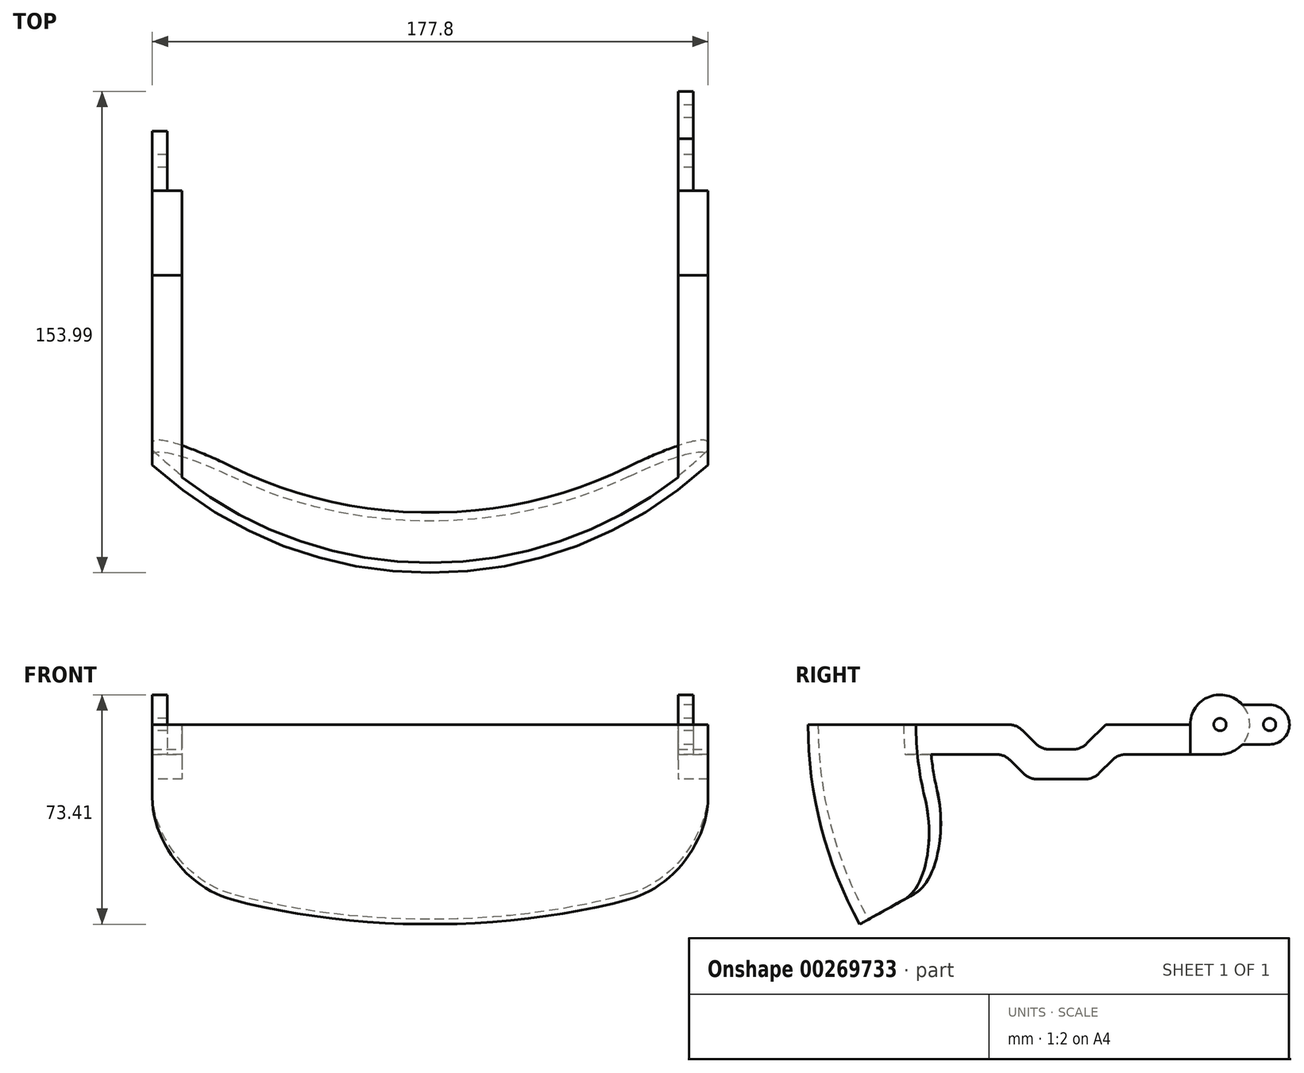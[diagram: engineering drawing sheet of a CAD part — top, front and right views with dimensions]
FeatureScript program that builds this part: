
annotation { "Feature Type Name" : "Feature", "Feature Type Description" : "" }
export const myFeature = defineFeature(function(context is Context, id is Id, definition is map)
    precondition{}
    {
        {
            var Q0;
            Q0=qCreatedBy(makeId("Right.planeOp"),FACE);
            var sketch = newSketch(context, id + "F0", { "sketchPlane" : qUnion([Q0])});
            skArc(sketch, "E0", {"start": v(0, 131.76) * mm, "mid": v(-131.76, 0) * mm, "end": v(0, -131.76) * mm});
            skArc(sketch, "E1", {"start": v(0, 128.59) * mm, "mid": v(-128.59, 0) * mm, "end": v(0, -128.59) * mm});
            skLineSegment(sketch, "E2", {"start": v(0, 131.76) * mm, "end": v(0, 0) * mm});
            skLineSegment(sketch, "E3.trimOffspring", {"start": v(0, -128.59) * mm, "end": v(0, -131.76) * mm});
            skPoint(sketch, "E4.orphan", {"position": v(0, 139.69) * mm});
            skSolve(sketch);
        }
        {
            var Q0;
            Q0 = qSketchRegion(id + "F0", true);
            var Q1;
            Q1=sQuery(id+"F0.wireOp",EDGE,"E2");
            revolve(context, id + "F1", {"entities" : qUnion([Q0]), "axis" : qUnion([Q1]), "revolveType" : RevolveType.FULL});
        }
        {
            var Q0;
            Q0=qCreatedBy(makeId("Front.planeOp"),FACE);
            var sketch = newSketch(context, id + "F2", { "sketchPlane" : qUnion([Q0])});
            skLineSegment(sketch, "E5.left", {"start": v(88.9, 154.45) * mm, "end": v(88.9, -154.45) * mm});
            skLineSegment(sketch, "E5.right", {"start": v(-88.9, 154.45) * mm, "end": v(-88.9, -154.45) * mm});
            skPoint(sketch, "E5.middle", {"position": v(0, 0) * mm});
            skLineSegment(sketch, "E6.bottom", {"start": v(198.77, 154.45) * mm, "end": v(88.9, 154.45) * mm});
            skLineSegment(sketch, "E6.top", {"start": v(198.77, -154.45) * mm, "end": v(88.9, -154.45) * mm});
            skLineSegment(sketch, "E6.left", {"start": v(198.77, 154.45) * mm, "end": v(198.77, -154.45) * mm});
            skLineSegment(sketch, "E6.right", {"start": v(-198.77, 154.45) * mm, "end": v(-198.77, -154.45) * mm});
            skLineSegment(sketch, "E7.trimOffspring", {"start": v(-88.9, 154.45) * mm, "end": v(-198.77, 154.45) * mm});
            skPoint(sketch, "E5.bottom.end.orphan", {"position": v(-88.9, 227.43) * mm});
            skPoint(sketch, "E5.bottom.start.orphan", {"position": v(88.9, 227.43) * mm});
            skLineSegment(sketch, "E8.trimOffspring", {"start": v(-88.9, -154.45) * mm, "end": v(-198.77, -154.45) * mm});
            skPoint(sketch, "E5.top.start.orphan", {"position": v(88.9, -227.43) * mm});
            skPoint(sketch, "E9.orphan", {"position": v(-88.9, -227.43) * mm});
            skSolve(sketch);
        }
        {
            var Q0;
            Q0 = qSketchRegion(id + "F2", true);
            extrude(context, id + "F3", {"entities" : qUnion([Q0]), "operationType" : NewBodyOperationType.REMOVE, "endBound" : BoundingType.SYMMETRIC, "depth" : 304.8 * mm});
        }
        {
            var Q0;
            Q0=qCreatedBy(makeId("Right.planeOp"),FACE);
            var sketch = newSketch(context, id + "F4", { "sketchPlane" : qUnion([Q0])});
            skLineSegment(sketch, "E10", {"start": v(0, 0) * mm, "end": v(-142.34, 0) * mm});
            skLineSegment(sketch, "E11", {"start": v(0, 0) * mm, "end": v(-124.79, -69.17) * mm});
            skArc(sketch, "E12", {"start": v(-124.79, -69.17) * mm, "mid": v(143.4, 35.68) * mm, "end": v(-142.34, 0) * mm});
            skSolve(sketch);
        }
        {
            var Q0;
            Q0 = qSketchRegion(id + "F4", true);
            extrude(context, id + "F5", {"entities" : qUnion([Q0]), "operationType" : NewBodyOperationType.REMOVE, "endBound" : BoundingType.SYMMETRIC, "depth" : 304.8 * mm});
        }
        {
            var Q0;
            Q0=makeQuery(id+"F5.boolean.opBoolean","INTERSECT",EDGE,{"derivedFrom":[makeQuery(id+"F3.boolean.opBoolean","COPY",FACE,{"derivedFrom":makeQuery(id+"F3.opExtrude","SWEPT_FACE",FACE,{"disambiguationData":[OSD([sQuery(id+"F2.wireOp",EDGE,"E5.left")])]})}),makeQuery(id+"F5.opExtrude","SWEPT_FACE",FACE,{"disambiguationData":[OSD([sQuery(id+"F4.wireOp",EDGE,"E11")])]})]});
            var Q1;
            Q1=makeQuery(id+"F5.boolean.opBoolean","INTERSECT",EDGE,{"derivedFrom":[makeQuery(id+"F3.boolean.opBoolean","COPY",FACE,{"derivedFrom":makeQuery(id+"F3.opExtrude","SWEPT_FACE",FACE,{"disambiguationData":[OSD([sQuery(id+"F2.wireOp",EDGE,"E5.right")])]})}),makeQuery(id+"F5.opExtrude","SWEPT_FACE",FACE,{"disambiguationData":[OSD([sQuery(id+"F4.wireOp",EDGE,"E11")])]})]});
            fillet(context, id + "F6", {"entities" : qUnion([Q0, Q1]), "radius" : 25.4 * mm, "tangentPropagation" : true, "allowEdgeOverflow" : false});
        }
        {
            var Q0;
            Q0=qCreatedBy(makeId("Front.planeOp"),FACE);
            var sketch = newSketch(context, id + "F7", { "sketchPlane" : qUnion([Q0])});
            skLineSegment(sketch, "E13", {"start": v(88.9, 0) * mm, "end": v(88.9, -9.53) * mm});
            skLineSegment(sketch, "E14", {"start": v(88.9, -9.53) * mm, "end": v(79.38, -9.53) * mm});
            skLineSegment(sketch, "E15", {"start": v(79.38, -9.53) * mm, "end": v(79.38, 0) * mm});
            skLineSegment(sketch, "E16", {"start": v(79.38, 0) * mm, "end": v(88.9, 0) * mm});
            skLineSegment(sketch, "E17", {"start": v(-79.38, 0) * mm, "end": v(-79.38, -9.53) * mm});
            skLineSegment(sketch, "E18", {"start": v(-79.38, -9.53) * mm, "end": v(-88.9, -9.53) * mm});
            skLineSegment(sketch, "E19", {"start": v(-88.9, -9.53) * mm, "end": v(-88.9, 0) * mm});
            skLineSegment(sketch, "E20", {"start": v(-88.9, 0) * mm, "end": v(-79.38, 0) * mm});
            skSolve(sketch);
        }
        {
            var Q0;
            Q0 = qSketchRegion(id + "F7", true);
            var Q1;
            Q1=makeQuery(id+"F1.opRevolve","SWEPT_FACE",FACE,{"disambiguationData":[OSD([sQuery(id+"F0.wireOp",EDGE,"E1")])]});
            extrude(context, id + "F8", {"entities" : qUnion([Q0]), "operationType" : NewBodyOperationType.ADD, "endBound" : BoundingType.UP_TO_SURFACE, "endBoundEntityFace" : qUnion([Q1]), "depth" : 25.4 * mm});
        }
        {
            var Q0;
            Q0=qCreatedBy(makeId("Right.planeOp"),FACE);
            var sketch = newSketch(context, id + "F9", { "sketchPlane" : qUnion([Q0])});
            skLineSegment(sketch, "E21", {"start": v(-23.04, 0) * mm, "end": v(-78.56, 0) * mm});
            skLineSegment(sketch, "E22", {"start": v(-41.28, -4.76) * mm, "end": v(-41.28, -9.52) * mm});
            skLineSegment(sketch, "E23", {"start": v(-60.33, -4.76) * mm, "end": v(-60.33, -7.94) * mm});
            skLineSegment(sketch, "E24", {"start": v(-64.92, -7.94) * mm, "end": v(-60.33, -7.94) * mm});
            skLineSegment(sketch, "E25", {"start": v(-41.28, -9.52) * mm, "end": v(-60.33, -9.52) * mm});
            skPoint(sketch, "E26.orphan", {"position": v(0, -4.76) * mm});
            skLineSegment(sketch, "E27", {"start": v(-60.33, -4.76) * mm, "end": v(-57.15, -7.94) * mm});
            skLineSegment(sketch, "E28", {"start": v(-41.28, -4.76) * mm, "end": v(-44.45, -7.94) * mm});
            skLineSegment(sketch, "E29", {"start": v(-78.56, 0) * mm, "end": v(-61.1, -17.46) * mm});
            skLineSegment(sketch, "E30", {"start": v(-23.04, 0) * mm, "end": v(-40.5, -17.46) * mm});
            skLineSegment(sketch, "E31", {"start": v(-61.1, -17.46) * mm, "end": v(-40.5, -17.46) * mm});
            skPoint(sketch, "E32.orphan", {"position": v(0, -9.52) * mm});
            skPoint(sketch, "E33.orphan", {"position": v(0, 0) * mm});
            skPoint(sketch, "E34.end.orphan", {"position": v(-36.51, 0) * mm});
            skLineSegment(sketch, "E35.trimOffspring", {"start": v(-57.15, -7.94) * mm, "end": v(-44.45, -7.94) * mm});
            skLineSegment(sketch, "E36.trimOffspring", {"start": v(-41.28, -7.94) * mm, "end": v(-36.6, -7.94) * mm});
            skSolve(sketch);
        }
        {
            var Q0;
            Q0 = qSketchRegion(id + "F9", true);
            extrude(context, id + "F10", {"entities" : qUnion([Q0]), "operationType" : NewBodyOperationType.ADD, "endBound" : BoundingType.SYMMETRIC, "depth" : 177.8 * mm});
        }
        {
            var Q0;
            Q0=makeQuery(id+"F10.boolean.opBoolean","MERGE",FACE,{"derivedFrom":[makeQuery(id+"F8.boolean.opBoolean","MERGE",FACE,{"derivedFrom":[makeQuery(id+"F3.boolean.opBoolean","COPY",FACE,{"derivedFrom":makeQuery(id+"F3.opExtrude","SWEPT_FACE",FACE,{"disambiguationData":[OSD([sQuery(id+"F2.wireOp",EDGE,"E5.left")])]})}),makeQuery(id+"F8.opExtrude","SWEPT_FACE",FACE,{"disambiguationData":[OSD([sQuery(id+"F7.wireOp",EDGE,"E13")])]})]}),makeQuery(id+"F10.opExtrude","CAP_FACE",FACE,{"disambiguationData":[OSD([sQuery(id+"F9.wireOp",EDGE,"E21"),sQuery(id+"F9.wireOp",EDGE,"E29"),sQuery(id+"F9.wireOp",EDGE,"E30"),sQuery(id+"F9.wireOp",EDGE,"E31")])],"isStart":false})]});
            var sketch = newSketch(context, id + "F11", { "sketchPlane" : qUnion([Q0])});
            skLineSegment(sketch, "E37", {"start": v(-36.51, 0) * mm, "end": v(-65.09, 0) * mm});
            skLineSegment(sketch, "E38", {"start": v(-57.15, -7.94) * mm, "end": v(-44.45, -7.94) * mm});
            skLineSegment(sketch, "E39", {"start": v(-60.33, -4.76) * mm, "end": v(-65.09, 0) * mm});
            skLineSegment(sketch, "E40", {"start": v(-41.28, -4.76) * mm, "end": v(-36.51, 0) * mm});
            skLineSegment(sketch, "E41", {"start": v(-60.33, -4.76) * mm, "end": v(-57.15, -7.94) * mm});
            skLineSegment(sketch, "E42", {"start": v(-41.28, -4.76) * mm, "end": v(-44.45, -7.94) * mm});
            skPoint(sketch, "E43.orphan", {"position": v(0, -4.76) * mm});
            skSolve(sketch);
        }
        {
            var Q0;
            Q0 = qSketchRegion(id + "F11", true);
            extrude(context, id + "F12", {"entities" : qUnion([Q0]), "operationType" : NewBodyOperationType.REMOVE, "oppositeDirection" : true, "depth" : 177.8 * mm});
        }
        {
            var Q0;
            Q0=qCreatedBy(makeId("Front.planeOp"),FACE);
            var sketch = newSketch(context, id + "F13", { "sketchPlane" : qUnion([Q0])});
            skLineSegment(sketch, "E44.bottom", {"start": v(-79.38, 25.4) * mm, "end": v(79.38, 25.4) * mm});
            skLineSegment(sketch, "E44.top", {"start": v(-79.38, -25.4) * mm, "end": v(79.38, -25.4) * mm});
            skLineSegment(sketch, "E44.left", {"start": v(-79.38, 25.4) * mm, "end": v(-79.38, -25.4) * mm});
            skLineSegment(sketch, "E44.right", {"start": v(79.38, 25.4) * mm, "end": v(79.38, -25.4) * mm});
            skPoint(sketch, "E44.middle", {"position": v(0, 0) * mm});
            skSolve(sketch);
        }
        {
            var Q0;
            Q0 = qSketchRegion(id + "F13", true);
            extrude(context, id + "F14", {"entities" : qUnion([Q0]), "operationType" : NewBodyOperationType.REMOVE, "depth" : 82.55 * mm});
        }
        {
            var Q0;
            Q0=makeQuery(id+"F10.boolean.opBoolean","MERGE",FACE,{"derivedFrom":[makeQuery(id+"F8.boolean.opBoolean","MERGE",FACE,{"derivedFrom":[makeQuery(id+"F3.boolean.opBoolean","COPY",FACE,{"derivedFrom":makeQuery(id+"F3.opExtrude","SWEPT_FACE",FACE,{"disambiguationData":[OSD([sQuery(id+"F2.wireOp",EDGE,"E5.right")])]})}),makeQuery(id+"F8.opExtrude","SWEPT_FACE",FACE,{"disambiguationData":[OSD([sQuery(id+"F7.wireOp",EDGE,"E19")])]})]}),makeQuery(id+"F10.opExtrude","CAP_FACE",FACE,{"disambiguationData":[OSD([sQuery(id+"F9.wireOp",EDGE,"E21"),sQuery(id+"F9.wireOp",EDGE,"E29"),sQuery(id+"F9.wireOp",EDGE,"E30"),sQuery(id+"F9.wireOp",EDGE,"E31")])],"isStart":true})]});
            var sketch = newSketch(context, id + "F15", { "sketchPlane" : qUnion([Q0])});
            skCircle(sketch, "E45", {"center": v(0, 0) * mm, "radius": 9.53 * mm});
            skSolve(sketch);
        }
        {
            var Q0;
            Q0 = qSketchRegion(id + "F15", true);
            extrude(context, id + "F16", {"entities" : qUnion([Q0]), "operationType" : NewBodyOperationType.ADD, "oppositeDirection" : true, "depth" : 4.76 * mm});
        }
        {
            var Q0;
            {var subQ7=sQuery(id+"F7.wireOp",EDGE,"E15");var subQ8=makeQuery(id+"F8.opExtrude","SWEPT_FACE",FACE,{"disambiguationData":[OSD([subQ7])]});Q0=makeQuery(id+"F14.boolean.opBoolean","MERGE",FACE,{"derivedFrom":[makeQuery(id+"F10.boolean.opBoolean","SPLIT",FACE,{"disambiguationData":[TD([makeQuery(id+"F10.opExtrude","SWEPT_FACE",FACE,{"disambiguationData":[OSD([sQuery(id+"F9.wireOp",EDGE,"E30")])]})])],"derivedFrom":subQ8}),makeQuery(id+"F10.boolean.opBoolean","SPLIT",FACE,{"disambiguationData":[TD([makeQuery(id+"F1.opRevolve","SWEPT_FACE",FACE,{"disambiguationData":[OSD([sQuery(id+"F0.wireOp",EDGE,"E1")])]})])],"derivedFrom":subQ8}),makeQuery(id+"F14.opExtrude","SWEPT_FACE",FACE,{"disambiguationData":[OSD([sQuery(id+"F13.wireOp",EDGE,"E44.right")])]})]});}
            var sketch = newSketch(context, id + "F17", { "sketchPlane" : qUnion([Q0])});
            skCircle(sketch, "E46", {"center": v(0, 0) * mm, "radius": 9.53 * mm});
            skSolve(sketch);
        }
        {
            var Q0;
            Q0 = qSketchRegion(id + "F17", true);
            extrude(context, id + "F18", {"entities" : qUnion([Q0]), "operationType" : NewBodyOperationType.ADD, "oppositeDirection" : true, "depth" : 4.76 * mm});
        }
        {
            var Q0;
            Q0=makeQuery(id+"F18.opExtrude","CAP_FACE",FACE,{"disambiguationData":[OSD([sQuery(id+"F17.wireOp",EDGE,"E46")])],"isStart":false});
            var sketch = newSketch(context, id + "F19", { "sketchPlane" : qUnion([Q0])});
            skArc(sketch, "E47", {"start": v(0, -9.53) * mm, "mid": v(6.74, 6.74) * mm, "end": v(-9.53, 0) * mm});
            skLineSegment(sketch, "E48", {"start": v(-9.53, 0) * mm, "end": v(-9.53, -9.53) * mm});
            skLineSegment(sketch, "E49", {"start": v(-9.53, -9.53) * mm, "end": v(0, -9.53) * mm});
            skSolve(sketch);
        }
        {
            var Q0;
            Q0 = qSketchRegion(id + "F19", true);
            extrude(context, id + "F20", {"entities" : qUnion([Q0]), "operationType" : NewBodyOperationType.REMOVE, "depth" : 4.76 * mm});
        }
        {
            var Q0;
            {var subQ7=sQuery(id+"F7.wireOp",EDGE,"E17");var subQ8=makeQuery(id+"F8.opExtrude","SWEPT_FACE",FACE,{"disambiguationData":[OSD([subQ7])]});Q0=makeQuery(id+"F14.boolean.opBoolean","MERGE",FACE,{"derivedFrom":[makeQuery(id+"F10.boolean.opBoolean","SPLIT",FACE,{"disambiguationData":[TD([makeQuery(id+"F10.opExtrude","SWEPT_FACE",FACE,{"disambiguationData":[OSD([sQuery(id+"F9.wireOp",EDGE,"E30")])]})])],"derivedFrom":subQ8}),makeQuery(id+"F10.boolean.opBoolean","SPLIT",FACE,{"disambiguationData":[TD([makeQuery(id+"F1.opRevolve","SWEPT_FACE",FACE,{"disambiguationData":[OSD([sQuery(id+"F0.wireOp",EDGE,"E1")])]})])],"derivedFrom":subQ8}),makeQuery(id+"F14.opExtrude","SWEPT_FACE",FACE,{"disambiguationData":[OSD([sQuery(id+"F13.wireOp",EDGE,"E44.left")])]})]});}
            var sketch = newSketch(context, id + "F21", { "sketchPlane" : qUnion([Q0])});
            skArc(sketch, "E50", {"start": v(0, -9.52) * mm, "mid": v(6.74, 6.74) * mm, "end": v(-9.53, 0) * mm});
            skLineSegment(sketch, "E51", {"start": v(-9.52, 0) * mm, "end": v(-9.52, -9.52) * mm});
            skLineSegment(sketch, "E52", {"start": v(-9.52, -9.52) * mm, "end": v(0, -9.52) * mm});
            skSolve(sketch);
        }
        {
            var Q0;
            Q0 = qSketchRegion(id + "F21", true);
            extrude(context, id + "F22", {"entities" : qUnion([Q0]), "operationType" : NewBodyOperationType.REMOVE, "oppositeDirection" : true, "depth" : 4.76 * mm});
        }
        {
            var Q0;
            Q0=qCreatedBy(makeId("Right.planeOp"),FACE);
            var sketch = newSketch(context, id + "F23", { "sketchPlane" : qUnion([Q0])});
            skCircle(sketch, "E53", {"center": v(0, 0) * mm, "radius": 2 * mm});
            skSolve(sketch);
        }
        {
            var Q0;
            Q0 = qSketchRegion(id + "F23", true);
            extrude(context, id + "F24", {"entities" : qUnion([Q0]), "operationType" : NewBodyOperationType.REMOVE, "endBound" : BoundingType.SYMMETRIC, "depth" : 177.8 * mm});
        }
        {
            var Q0;
            {var subQ0=sQuery(id+"F7.wireOp",EDGE,"E13");var subQ1=sQuery(id+"F4.wireOp",EDGE,"E10");var subQ2=sQuery(id+"F2.wireOp",EDGE,"E5.left");var subQ3=sQuery(id+"F7.wireOp",EDGE,"E16");var subQ4=sQuery(id+"F11.wireOp",EDGE,"E39");Q0=makeQuery(id+"F14.boolean.opBoolean","SPLIT",EDGE,{"disambiguationData":[TD([makeQuery(id+"F3.boolean.opBoolean","COPY",FACE,{"derivedFrom":makeQuery(id+"F3.opExtrude","SWEPT_FACE",FACE,{"disambiguationData":[OSD([subQ2])]})})])],"derivedFrom":makeQuery(id+"F12.boolean.opBoolean","COPY",EDGE,{"derivedFrom":makeQuery(id+"F12.opExtrude","SWEPT_EDGE",EDGE,{"disambiguationData":[OSD([subQ2,subQ1,subQ0,subQ3,sQuery(id+"F11.wireOp",EDGE,"E37"),subQ4])]})})});}
            var Q1;
            {var subQ0=sQuery(id+"F11.wireOp",EDGE,"E38");var subQ1=sQuery(id+"F11.wireOp",EDGE,"E41");Q1=makeQuery(id+"F14.boolean.opBoolean","SPLIT",EDGE,{"disambiguationData":[TD([makeQuery(id+"F3.boolean.opBoolean","COPY",FACE,{"derivedFrom":makeQuery(id+"F3.opExtrude","SWEPT_FACE",FACE,{"disambiguationData":[OSD([sQuery(id+"F2.wireOp",EDGE,"E5.left")])]})})])],"derivedFrom":makeQuery(id+"F12.boolean.opBoolean","COPY",EDGE,{"derivedFrom":makeQuery(id+"F12.opExtrude","SWEPT_EDGE",EDGE,{"disambiguationData":[OSD([subQ0,subQ1])]})})});}
            var Q2;
            {var subQ0=sQuery(id+"F11.wireOp",EDGE,"E38");var subQ1=sQuery(id+"F11.wireOp",EDGE,"E42");Q2=makeQuery(id+"F14.boolean.opBoolean","SPLIT",EDGE,{"disambiguationData":[TD([makeQuery(id+"F3.boolean.opBoolean","COPY",FACE,{"derivedFrom":makeQuery(id+"F3.opExtrude","SWEPT_FACE",FACE,{"disambiguationData":[OSD([sQuery(id+"F2.wireOp",EDGE,"E5.left")])]})})])],"derivedFrom":makeQuery(id+"F12.boolean.opBoolean","COPY",EDGE,{"derivedFrom":makeQuery(id+"F12.opExtrude","SWEPT_EDGE",EDGE,{"disambiguationData":[OSD([subQ0,subQ1])]})})});}
            var Q3;
            {var subQ0=sQuery(id+"F7.wireOp",EDGE,"E13");var subQ1=sQuery(id+"F4.wireOp",EDGE,"E10");var subQ2=sQuery(id+"F2.wireOp",EDGE,"E5.left");var subQ3=sQuery(id+"F7.wireOp",EDGE,"E16");var subQ5=sQuery(id+"F11.wireOp",EDGE,"E40");Q3=makeQuery(id+"F14.boolean.opBoolean","SPLIT",EDGE,{"disambiguationData":[TD([makeQuery(id+"F3.boolean.opBoolean","COPY",FACE,{"derivedFrom":makeQuery(id+"F3.opExtrude","SWEPT_FACE",FACE,{"disambiguationData":[OSD([subQ2])]})})])],"derivedFrom":makeQuery(id+"F12.boolean.opBoolean","COPY",EDGE,{"derivedFrom":makeQuery(id+"F12.opExtrude","SWEPT_EDGE",EDGE,{"disambiguationData":[OSD([subQ2,subQ1,subQ0,subQ3,sQuery(id+"F11.wireOp",EDGE,"E37"),subQ5])]})})});}
            var Q4;
            Q4=makeQuery(id+"F20.boolean.opBoolean","COPY",EDGE,{"derivedFrom":makeQuery(id+"F20.opExtrude","CAP_EDGE",EDGE,{"disambiguationData":[OSD([sQuery(id+"F19.wireOp",EDGE,"E48")])],"isStart":false})});
            var Q5;
            Q5=makeQuery(id+"F10.boolean.opBoolean","INTERSECT",EDGE,{"derivedFrom":[makeQuery(id+"F8.opExtrude","SWEPT_FACE",FACE,{"disambiguationData":[OSD([sQuery(id+"F7.wireOp",EDGE,"E14")])]}),makeQuery(id+"F10.opExtrude","SWEPT_FACE",FACE,{"disambiguationData":[OSD([sQuery(id+"F9.wireOp",EDGE,"E30")])]})]});
            var Q6;
            {var subQ0=sQuery(id+"F9.wireOp",EDGE,"E31");var subQ1=sQuery(id+"F9.wireOp",EDGE,"E30");Q6=makeQuery(id+"F14.boolean.opBoolean","SPLIT",EDGE,{"disambiguationData":[TD([makeQuery(id+"F3.boolean.opBoolean","COPY",FACE,{"derivedFrom":makeQuery(id+"F3.opExtrude","SWEPT_FACE",FACE,{"disambiguationData":[OSD([sQuery(id+"F2.wireOp",EDGE,"E5.left")])]})})])],"derivedFrom":makeQuery(id+"F10.opExtrude","SWEPT_EDGE",EDGE,{"disambiguationData":[OSD([subQ1,subQ0])]})});}
            var Q7;
            {var subQ0=sQuery(id+"F9.wireOp",EDGE,"E31");var subQ1=sQuery(id+"F9.wireOp",EDGE,"E29");Q7=makeQuery(id+"F14.boolean.opBoolean","SPLIT",EDGE,{"disambiguationData":[TD([makeQuery(id+"F3.boolean.opBoolean","COPY",FACE,{"derivedFrom":makeQuery(id+"F3.opExtrude","SWEPT_FACE",FACE,{"disambiguationData":[OSD([sQuery(id+"F2.wireOp",EDGE,"E5.left")])]})})])],"derivedFrom":makeQuery(id+"F10.opExtrude","SWEPT_EDGE",EDGE,{"disambiguationData":[OSD([subQ1,subQ0])]})});}
            var Q8;
            Q8=makeQuery(id+"F10.boolean.opBoolean","INTERSECT",EDGE,{"derivedFrom":[makeQuery(id+"F8.opExtrude","SWEPT_FACE",FACE,{"disambiguationData":[OSD([sQuery(id+"F7.wireOp",EDGE,"E14")])]}),makeQuery(id+"F10.opExtrude","SWEPT_FACE",FACE,{"disambiguationData":[OSD([sQuery(id+"F9.wireOp",EDGE,"E29")])]})]});
            var Q9;
            Q9=makeQuery(id+"F8.opExtrude","TWEAK_EDGE",EDGE,{"derivedFrom":[makeQuery(id+"F1.opRevolve","SWEPT_FACE",FACE,{"disambiguationData":[OSD([sQuery(id+"F0.wireOp",EDGE,"E1")])]}),makeQuery(id+"F7.imprint","IMPRINT",EDGE,{"derivedFrom":sQuery(id+"F7.wireOp",EDGE,"E14")})]});
            var Q10;
            {var subQ0=sQuery(id+"F7.wireOp",EDGE,"E16");var subQ1=sQuery(id+"F11.wireOp",EDGE,"E39");var subQ3=sQuery(id+"F4.wireOp",EDGE,"E10");Q10=makeQuery(id+"F14.boolean.opBoolean","SPLIT",EDGE,{"disambiguationData":[TD([makeQuery(id+"F3.boolean.opBoolean","COPY",FACE,{"derivedFrom":makeQuery(id+"F3.opExtrude","SWEPT_FACE",FACE,{"disambiguationData":[OSD([sQuery(id+"F2.wireOp",EDGE,"E5.right")])]})})])],"derivedFrom":makeQuery(id+"F12.boolean.opBoolean","COPY",EDGE,{"derivedFrom":makeQuery(id+"F12.opExtrude","SWEPT_EDGE",EDGE,{"disambiguationData":[OSD([sQuery(id+"F2.wireOp",EDGE,"E5.left"),subQ3,sQuery(id+"F7.wireOp",EDGE,"E13"),subQ0,sQuery(id+"F11.wireOp",EDGE,"E37"),subQ1])]})})});}
            var Q11;
            {var subQ0=sQuery(id+"F11.wireOp",EDGE,"E38");var subQ1=sQuery(id+"F11.wireOp",EDGE,"E41");Q11=makeQuery(id+"F14.boolean.opBoolean","SPLIT",EDGE,{"disambiguationData":[TD([makeQuery(id+"F3.boolean.opBoolean","COPY",FACE,{"derivedFrom":makeQuery(id+"F3.opExtrude","SWEPT_FACE",FACE,{"disambiguationData":[OSD([sQuery(id+"F2.wireOp",EDGE,"E5.right")])]})})])],"derivedFrom":makeQuery(id+"F12.boolean.opBoolean","COPY",EDGE,{"derivedFrom":makeQuery(id+"F12.opExtrude","SWEPT_EDGE",EDGE,{"disambiguationData":[OSD([subQ0,subQ1])]})})});}
            var Q12;
            {var subQ0=sQuery(id+"F11.wireOp",EDGE,"E42");var subQ1=sQuery(id+"F11.wireOp",EDGE,"E38");Q12=makeQuery(id+"F14.boolean.opBoolean","SPLIT",EDGE,{"disambiguationData":[TD([makeQuery(id+"F3.boolean.opBoolean","COPY",FACE,{"derivedFrom":makeQuery(id+"F3.opExtrude","SWEPT_FACE",FACE,{"disambiguationData":[OSD([sQuery(id+"F2.wireOp",EDGE,"E5.right")])]})})])],"derivedFrom":makeQuery(id+"F12.boolean.opBoolean","COPY",EDGE,{"derivedFrom":makeQuery(id+"F12.opExtrude","SWEPT_EDGE",EDGE,{"disambiguationData":[OSD([subQ1,subQ0])]})})});}
            var Q13;
            {var subQ0=sQuery(id+"F7.wireOp",EDGE,"E16");var subQ2=sQuery(id+"F11.wireOp",EDGE,"E40");var subQ3=sQuery(id+"F4.wireOp",EDGE,"E10");Q13=makeQuery(id+"F14.boolean.opBoolean","SPLIT",EDGE,{"disambiguationData":[TD([makeQuery(id+"F3.boolean.opBoolean","COPY",FACE,{"derivedFrom":makeQuery(id+"F3.opExtrude","SWEPT_FACE",FACE,{"disambiguationData":[OSD([sQuery(id+"F2.wireOp",EDGE,"E5.right")])]})})])],"derivedFrom":makeQuery(id+"F12.boolean.opBoolean","COPY",EDGE,{"derivedFrom":makeQuery(id+"F12.opExtrude","SWEPT_EDGE",EDGE,{"disambiguationData":[OSD([sQuery(id+"F2.wireOp",EDGE,"E5.left"),subQ3,sQuery(id+"F7.wireOp",EDGE,"E13"),subQ0,sQuery(id+"F11.wireOp",EDGE,"E37"),subQ2])]})})});}
            var Q14;
            Q14=makeQuery(id+"F10.boolean.opBoolean","INTERSECT",EDGE,{"derivedFrom":[makeQuery(id+"F8.opExtrude","SWEPT_FACE",FACE,{"disambiguationData":[OSD([sQuery(id+"F7.wireOp",EDGE,"E18")])]}),makeQuery(id+"F10.opExtrude","SWEPT_FACE",FACE,{"disambiguationData":[OSD([sQuery(id+"F9.wireOp",EDGE,"E30")])]})]});
            var Q15;
            {var subQ0=sQuery(id+"F9.wireOp",EDGE,"E31");var subQ1=sQuery(id+"F9.wireOp",EDGE,"E30");Q15=makeQuery(id+"F14.boolean.opBoolean","SPLIT",EDGE,{"disambiguationData":[TD([makeQuery(id+"F3.boolean.opBoolean","COPY",FACE,{"derivedFrom":makeQuery(id+"F3.opExtrude","SWEPT_FACE",FACE,{"disambiguationData":[OSD([sQuery(id+"F2.wireOp",EDGE,"E5.right")])]})})])],"derivedFrom":makeQuery(id+"F10.opExtrude","SWEPT_EDGE",EDGE,{"disambiguationData":[OSD([subQ1,subQ0])]})});}
            var Q16;
            {var subQ0=sQuery(id+"F9.wireOp",EDGE,"E29");var subQ1=sQuery(id+"F9.wireOp",EDGE,"E31");Q16=makeQuery(id+"F14.boolean.opBoolean","SPLIT",EDGE,{"disambiguationData":[TD([makeQuery(id+"F3.boolean.opBoolean","COPY",FACE,{"derivedFrom":makeQuery(id+"F3.opExtrude","SWEPT_FACE",FACE,{"disambiguationData":[OSD([sQuery(id+"F2.wireOp",EDGE,"E5.right")])]})})])],"derivedFrom":makeQuery(id+"F10.opExtrude","SWEPT_EDGE",EDGE,{"disambiguationData":[OSD([subQ0,subQ1])]})});}
            var Q17;
            Q17=makeQuery(id+"F10.boolean.opBoolean","INTERSECT",EDGE,{"derivedFrom":[makeQuery(id+"F8.opExtrude","SWEPT_FACE",FACE,{"disambiguationData":[OSD([sQuery(id+"F7.wireOp",EDGE,"E18")])]}),makeQuery(id+"F10.opExtrude","SWEPT_FACE",FACE,{"disambiguationData":[OSD([sQuery(id+"F9.wireOp",EDGE,"E29")])]})]});
            var Q18;
            Q18=makeQuery(id+"F8.opExtrude","TWEAK_EDGE",EDGE,{"derivedFrom":[makeQuery(id+"F1.opRevolve","SWEPT_FACE",FACE,{"disambiguationData":[OSD([sQuery(id+"F0.wireOp",EDGE,"E1")])]}),makeQuery(id+"F7.imprint","IMPRINT",EDGE,{"derivedFrom":sQuery(id+"F7.wireOp",EDGE,"E18")})]});
            var Q19;
            Q19=makeQuery(id+"F22.boolean.opBoolean","COPY",EDGE,{"derivedFrom":makeQuery(id+"F22.opExtrude","CAP_EDGE",EDGE,{"disambiguationData":[OSD([sQuery(id+"F21.wireOp",EDGE,"E51")])],"isStart":true})});
            fillet(context, id + "F25", {"entities" : qUnion([Q0, Q1, Q2, Q3, Q4, Q5, Q6, Q7, Q8, Q9, Q10, Q11, Q12, Q13, Q14, Q15, Q16, Q17, Q18, Q19]), "radius" : 6.35 * mm, "tangentPropagation" : true, "allowEdgeOverflow" : false});
        }
        {
            var Q0;
            {var subQ7=sQuery(id+"F7.wireOp",EDGE,"E15");var subQ8=makeQuery(id+"F8.opExtrude","SWEPT_FACE",FACE,{"disambiguationData":[OSD([subQ7])]});Q0=makeQuery(id+"F18.boolean.opBoolean","MERGE",FACE,{"derivedFrom":[makeQuery(id+"F14.boolean.opBoolean","MERGE",FACE,{"derivedFrom":[makeQuery(id+"F10.boolean.opBoolean","SPLIT",FACE,{"disambiguationData":[TD([makeQuery(id+"F10.opExtrude","SWEPT_FACE",FACE,{"disambiguationData":[OSD([sQuery(id+"F9.wireOp",EDGE,"E30")])]})])],"derivedFrom":subQ8}),makeQuery(id+"F10.boolean.opBoolean","SPLIT",FACE,{"disambiguationData":[TD([makeQuery(id+"F1.opRevolve","SWEPT_FACE",FACE,{"disambiguationData":[OSD([sQuery(id+"F0.wireOp",EDGE,"E1")])]})])],"derivedFrom":subQ8}),makeQuery(id+"F14.opExtrude","SWEPT_FACE",FACE,{"disambiguationData":[OSD([sQuery(id+"F13.wireOp",EDGE,"E44.right")])]})]}),makeQuery(id+"F18.opExtrude","CAP_FACE",FACE,{"disambiguationData":[OSD([sQuery(id+"F17.wireOp",EDGE,"E46")])],"isStart":true})]});}
            var sketch = newSketch(context, id + "F26", { "sketchPlane" : qUnion([Q0])});
            skLineSegment(sketch, "E54.bottom", {"start": v(-15.88, -6.35) * mm, "end": v(0, -6.35) * mm});
            skLineSegment(sketch, "E54.top", {"start": v(-15.88, 6.35) * mm, "end": v(0, 6.35) * mm});
            skPoint(sketch, "E54.middle", {"position": v(0, 0) * mm});
            skArc(sketch, "E55", {"start": v(0, 2) * mm, "mid": v(-2, 0) * mm, "end": v(0, -2) * mm});
            skLineSegment(sketch, "E56", {"start": v(0, 6.35) * mm, "end": v(0, 2) * mm});
            skPoint(sketch, "E57", {"position": v(-15.88, 6.35) * mm});
            skArc(sketch, "E58", {"start": v(-15.88, 6.35) * mm, "mid": v(-22.23, 0) * mm, "end": v(-15.88, -6.35) * mm});
            skPoint(sketch, "E59.orphan", {"position": v(-22.23, 6.35) * mm});
            skPoint(sketch, "E60.orphan", {"position": v(-22.23, -6.35) * mm});
            skPoint(sketch, "E54.right.end.orphan", {"position": v(22.23, 6.35) * mm});
            skPoint(sketch, "E61.orphan", {"position": v(22.23, -6.35) * mm});
            skLineSegment(sketch, "E62.trimOffspring", {"start": v(0, -2) * mm, "end": v(0, -6.35) * mm});
            skCircle(sketch, "E63", {"center": v(-15.88, 0) * mm, "radius": 2 * mm});
            skSolve(sketch);
        }
        {
            var Q0;
            Q0 = qSketchRegion(id + "F26", true);
            extrude(context, id + "F27", {"entities" : qUnion([Q0]), "operationType" : NewBodyOperationType.ADD, "oppositeDirection" : true, "depth" : 4.76 * mm});
        }
    });
